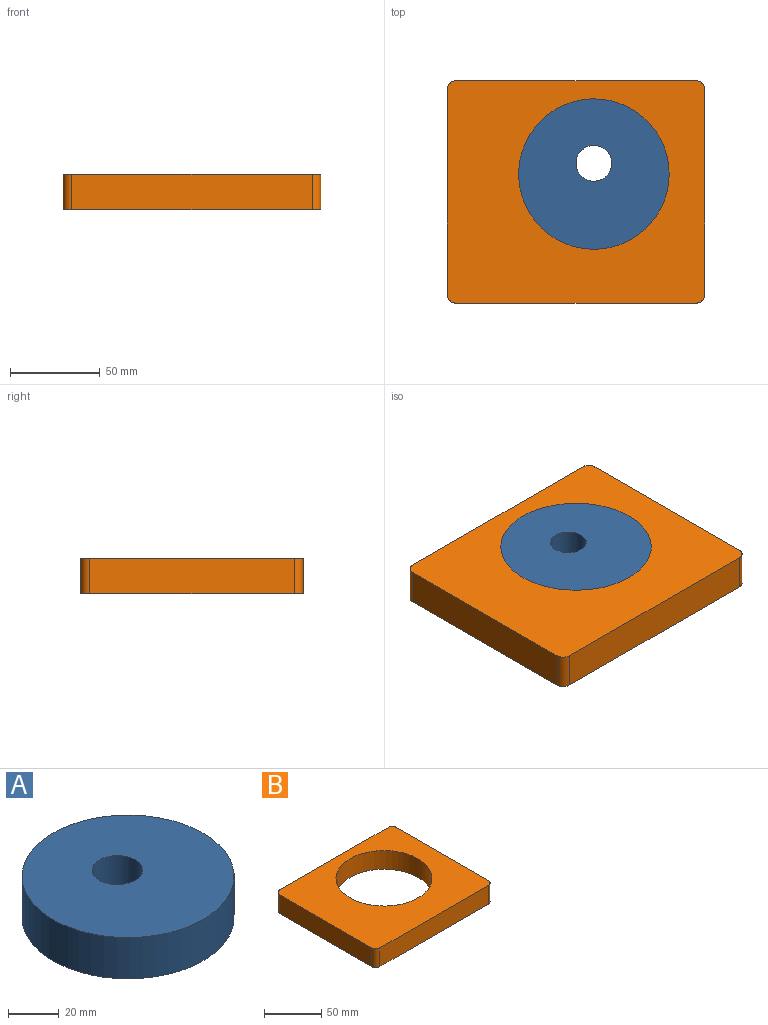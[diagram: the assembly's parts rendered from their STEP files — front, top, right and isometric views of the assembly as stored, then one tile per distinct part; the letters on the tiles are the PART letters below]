
ASSEMBLY  parts=2 mates=1
PART A: 4 faces, bbox 84x84x20 mm
  f0: cylinder r=10mm len=20mm, axis (0,0,-1), area 1256.6mm2, adj f2,f3
  f1: cylinder r=42mm len=84mm, axis (0,0,-1), area 5277.9mm2, adj f2,f3
  f2: plane 84x84mm, normal (0,0,1), area 5227.6mm2, adj f0,f1
  f3: plane 84x84mm, normal (0,0,-1), area 5227.6mm2, adj f0,f1
PART B: 11 faces, bbox 144x124x20 mm
  f0: plane 114x20mm, normal (1,0,0), area 2280mm2, adj f1,f8,f9,f10
  f1: cylinder r=5mm len=20mm, axis (0,0,-1), area 157.1mm2, adj f0,f2,f9,f10
  f2: plane 134x20mm, normal (0,1,0), area 2680mm2, adj f1,f3,f9,f10
  f3: cylinder r=5mm len=20mm, axis (0,0,-1), area 157.1mm2, adj f2,f4,f9,f10
  f4: plane 114x20mm, normal (-1,0,0), area 2280mm2, adj f3,f5,f9,f10
  f5: cylinder r=5mm len=20mm, axis (0,0,-1), area 157.1mm2, adj f4,f6,f9,f10
  f6: plane 134x20mm, normal (0,-1,0), area 2680mm2, adj f5,f8,f9,f10
  f7: cylinder r=42mm len=84mm, axis (0,0,-1), area 5277.9mm2, adj f9,f10
  f8: cylinder r=5mm len=20mm, axis (0,0,-1), area 157.1mm2, adj f0,f6,f9,f10
  f9: plane 144x124mm, normal (0,0,1), area 12292.8mm2, adj f0,f1,f2,f3,f4,f5,f6,f7
  f10: plane 144x124mm, normal (0,0,-1), area 12292.8mm2, adj f0,f1,f2,f3,f4,f5,f6,f7
PLACE A t=(-26.22,77.21,15.97)mm
PLACE B t=(-26.22,77.21,15.97)mm
MATE revolute A.f1 <-> B.f7  axis (0,0,-1) through (-26.22,77.21,25.97)mm
